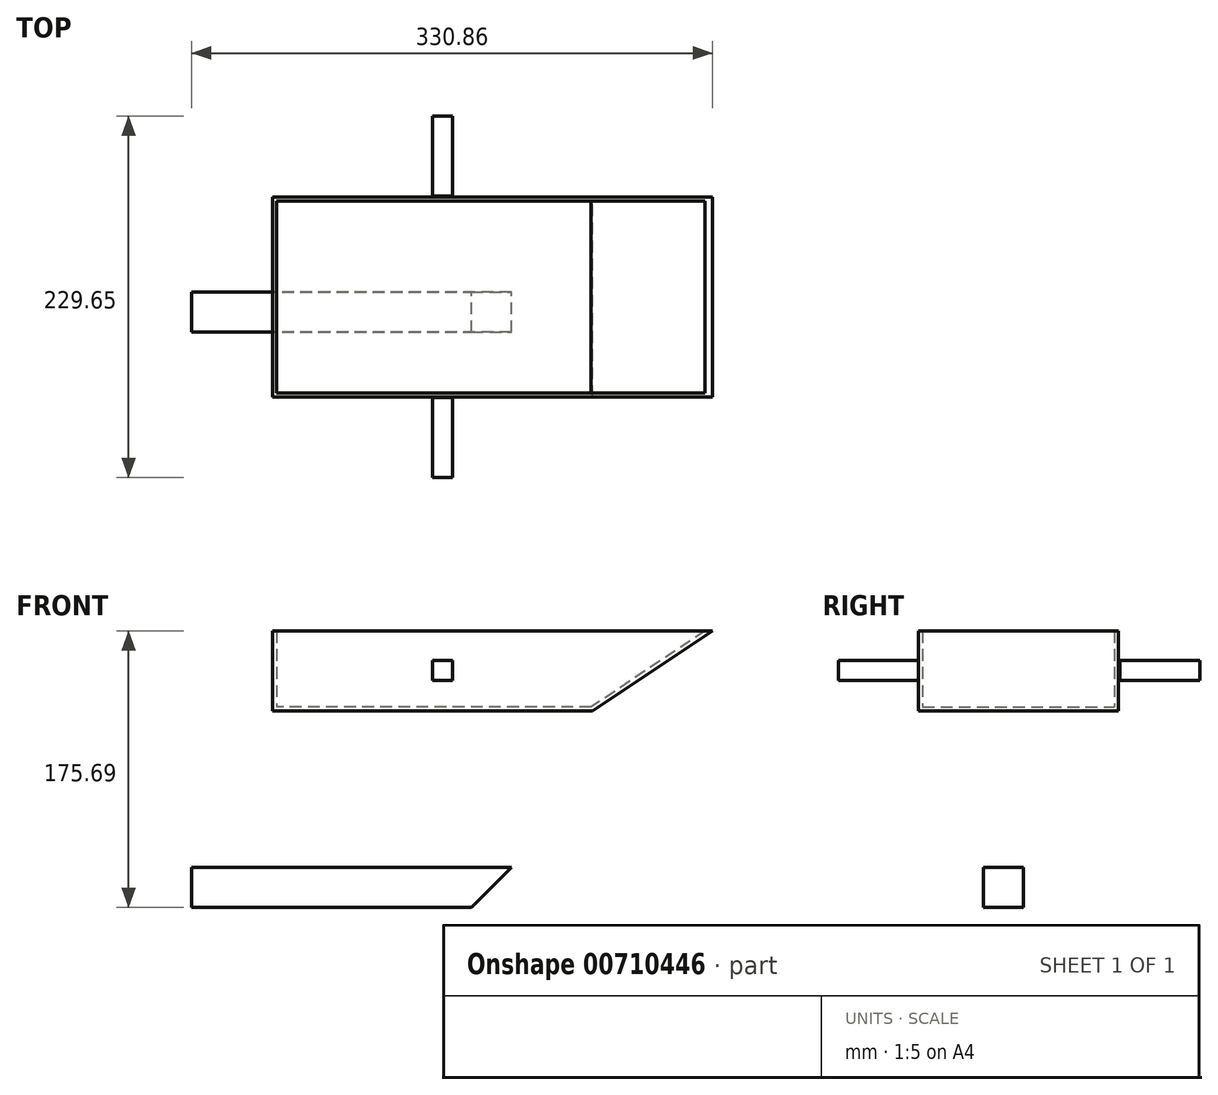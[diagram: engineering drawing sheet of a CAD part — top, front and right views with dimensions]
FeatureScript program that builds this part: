
annotation { "Feature Type Name" : "Feature", "Feature Type Description" : "" }
export const myFeature = defineFeature(function(context is Context, id is Id, definition is map)
    precondition{}
    {
        {
            var Q0;
            Q0=qCreatedBy(makeId("Front.planeOp"),FACE);
            var sketch = newSketch(context, id + "F0", { "sketchPlane" : qUnion([Q0])});
            skLineSegment(sketch, "E0.bottom", {"start": v(101.6, 25.4) * mm, "end": v(-101.6, 25.4) * mm});
            skLineSegment(sketch, "E0.top", {"start": v(101.6, -25.4) * mm, "end": v(-101.6, -25.4) * mm});
            skLineSegment(sketch, "E0.left", {"start": v(101.6, 25.4) * mm, "end": v(101.6, -25.4) * mm});
            skLineSegment(sketch, "E0.right", {"start": v(-101.6, 25.4) * mm, "end": v(-101.6, -25.4) * mm});
            skPoint(sketch, "E0.middle", {"position": v(0, 0) * mm});
            skLineSegment(sketch, "E1", {"start": v(101.6, 25.4) * mm, "end": v(177.8, 25.4) * mm});
            skLineSegment(sketch, "E2", {"start": v(177.8, 25.4) * mm, "end": v(101.6, -25.4) * mm});
            skSolve(sketch);
        }
        {
            var Q0;
            Q0=makeQuery(id+"F0.imprint","IMPRINT",FACE,{"disambiguationData":[TD([[makeQuery(id+"F0.imprint","IMPRINT",EDGE,{"derivedFrom":sQuery(id+"F0.wireOp",EDGE,"E0.left")}),1.0]])]});
            var Q1;
            Q1=makeQuery(id+"F0.imprint","IMPRINT",FACE,{"disambiguationData":[TD([[makeQuery(id+"F0.imprint","IMPRINT",EDGE,{"derivedFrom":sQuery(id+"F0.wireOp",EDGE,"E0.bottom")}),1.0]])]});
            extrude(context, id + "F1", {"entities" : qUnion([Q0, Q1]), "endBound" : BoundingType.SYMMETRIC, "depth" : 6.35 * mm, "offsetDistance" : 25.4 * mm});
        }
        {
            var Q0;
            Q0=makeQuery(id+"F1.opExtrude","SWEPT_BODY",BODY,{"disambiguationData":[OSD([sQuery(id+"F0.wireOp",EDGE,"E0.bottom"),sQuery(id+"F0.wireOp",EDGE,"E0.top"),sQuery(id+"F0.wireOp",EDGE,"E0.right"),sQuery(id+"F0.wireOp",EDGE,"E1"),sQuery(id+"F0.wireOp",EDGE,"E2")])]});
            transform(context, id + "F2", {"entities" : qUnion([Q0]), "transformType" : TransformType.COPY});
        }
        {
            var Q0;
            Q0=makeQuery(id+"F2.opPattern","COPY",BODY,{"derivedFrom":makeQuery(id+"F1.opExtrude","SWEPT_BODY",BODY,{"disambiguationData":[OSD([sQuery(id+"F0.wireOp",EDGE,"E0.bottom"),sQuery(id+"F0.wireOp",EDGE,"E0.top"),sQuery(id+"F0.wireOp",EDGE,"E0.right"),sQuery(id+"F0.wireOp",EDGE,"E1"),sQuery(id+"F0.wireOp",EDGE,"E2")])]}),"instanceName":"1"});
            deleteBodies(context, id + "F3", {"entities" : qUnion([Q0])});
        }
        {
            var Q0;
            Q0=makeQuery(id+"F1.opExtrude","CAP_FACE",FACE,{"disambiguationData":[OSD([sQuery(id+"F0.wireOp",EDGE,"E0.bottom"),sQuery(id+"F0.wireOp",EDGE,"E0.top"),sQuery(id+"F0.wireOp",EDGE,"E0.right"),sQuery(id+"F0.wireOp",EDGE,"E1"),sQuery(id+"F0.wireOp",EDGE,"E2")])],"isStart":false});
            extrude(context, id + "F4", {"entities" : qUnion([Q0]), "operationType" : NewBodyOperationType.ADD, "endBound" : BoundingType.SYMMETRIC, "depth" : 127 * mm, "offsetDistance" : 25.4 * mm});
        }
        {
            var Q0;
            {var subQ0=sQuery(id+"F0.wireOp",EDGE,"E1");var subQ1=sQuery(id+"F0.wireOp",EDGE,"E0.bottom");Q0=makeQuery(id+"F4.boolean.opBoolean","MERGE",FACE,{"derivedFrom":[makeQuery(id+"F1.opExtrude","SWEPT_FACE",FACE,{"disambiguationData":[OSD([subQ1,subQ0])]}),makeQuery(id+"F4.opExtrude","SWEPT_FACE",FACE,{"disambiguationData":[OSD([subQ1,subQ0])]})]});}
            shell(context, id + "F5", {"entities" : qUnion([Q0]), "thickness" : 2.54 * mm});
        }
        {
            var Q0;
            Q0=qCreatedBy(makeId("Right.planeOp"),FACE);
            var sketch = newSketch(context, id + "F6", { "sketchPlane" : qUnion([Q0])});
            skLineSegment(sketch, "E3.bottom", {"start": v(-66.84, -5.87) * mm, "end": v(-117.64, -5.87) * mm});
            skLineSegment(sketch, "E3.top", {"start": v(-66.84, 6.83) * mm, "end": v(-117.64, 6.83) * mm});
            skLineSegment(sketch, "E3.left", {"start": v(-66.84, -5.87) * mm, "end": v(-66.84, 6.83) * mm});
            skLineSegment(sketch, "E3.right", {"start": v(-117.64, -5.87) * mm, "end": v(-117.64, 6.83) * mm});
            skLineSegment(sketch, "E4.bottom", {"start": v(61.21, -5.87) * mm, "end": v(112.01, -5.87) * mm});
            skLineSegment(sketch, "E4.top", {"start": v(61.21, 6.83) * mm, "end": v(112.01, 6.83) * mm});
            skLineSegment(sketch, "E4.left", {"start": v(61.21, -5.87) * mm, "end": v(61.21, 6.83) * mm});
            skLineSegment(sketch, "E4.right", {"start": v(112.01, -5.87) * mm, "end": v(112.01, 6.83) * mm});
            skSolve(sketch);
        }
        {
            var Q0;
            Q0 = qSketchRegion(id + "F6", true);
            extrude(context, id + "F7", {"entities" : qUnion([Q0]), "depth" : 12.7 * mm, "offsetDistance" : 25.4 * mm});
        }
        {
            var Q0;
            Q0=qCreatedBy(makeId("Front.planeOp"),FACE);
            var sketch = newSketch(context, id + "F8", { "sketchPlane" : qUnion([Q0])});
            skLineSegment(sketch, "E5.bottom", {"start": v(-153.06, -124.89) * mm, "end": v(24.74, -124.89) * mm});
            skLineSegment(sketch, "E5.top", {"start": v(-153.06, -150.29) * mm, "end": v(24.74, -150.29) * mm});
            skLineSegment(sketch, "E5.left", {"start": v(-153.06, -124.89) * mm, "end": v(-153.06, -150.29) * mm});
            skLineSegment(sketch, "E5.right", {"start": v(24.74, -124.89) * mm, "end": v(24.74, -150.29) * mm});
            skLineSegment(sketch, "E6", {"start": v(24.74, -150.29) * mm, "end": v(50.14, -124.89) * mm});
            skLineSegment(sketch, "E7", {"start": v(50.14, -124.89) * mm, "end": v(24.74, -124.89) * mm});
            skSolve(sketch);
        }
        {
            var Q0;
            Q0=makeQuery(id+"F8.imprint","IMPRINT",FACE,{"disambiguationData":[TD([[makeQuery(id+"F8.imprint","IMPRINT",EDGE,{"derivedFrom":sQuery(id+"F8.wireOp",EDGE,"E5.right")}),1.0]])]});
            var Q1;
            Q1=makeQuery(id+"F8.imprint","IMPRINT",FACE,{"disambiguationData":[TD([[makeQuery(id+"F8.imprint","IMPRINT",EDGE,{"derivedFrom":sQuery(id+"F8.wireOp",EDGE,"E5.bottom")}),-1.0]])]});
            extrude(context, id + "F9", {"entities" : qUnion([Q0, Q1]), "depth" : 25.4 * mm, "offsetDistance" : 25.4 * mm});
        }
    });
